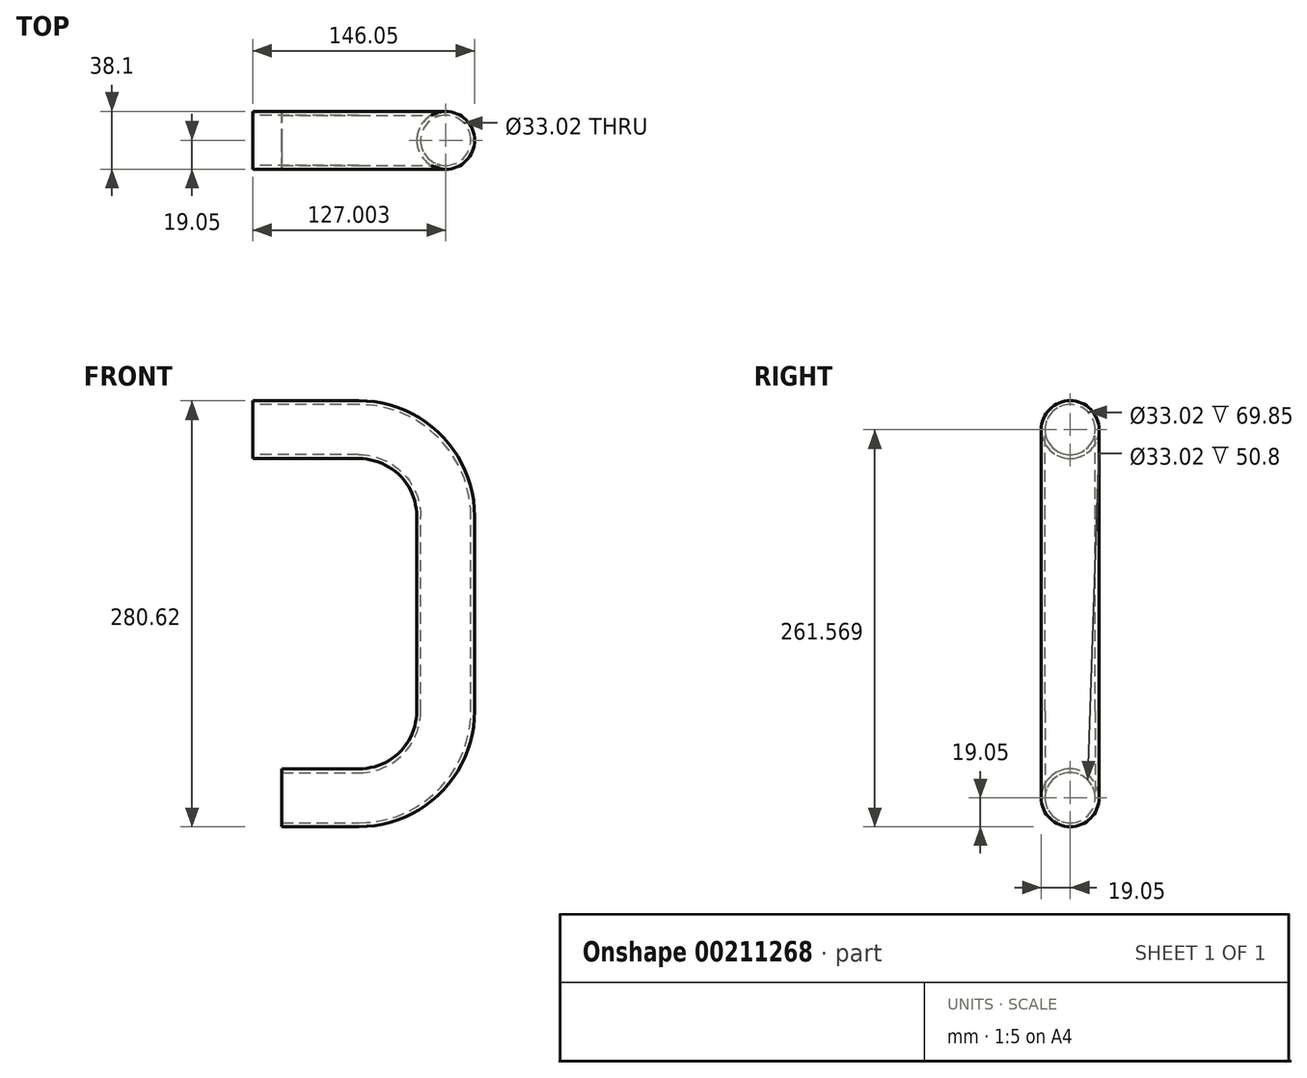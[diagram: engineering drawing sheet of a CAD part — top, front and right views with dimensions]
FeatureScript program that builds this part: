
annotation { "Feature Type Name" : "Feature", "Feature Type Description" : "" }
export const myFeature = defineFeature(function(context is Context, id is Id, definition is map)
    precondition{}
    {
        {
            var Q0;
            Q0=qCreatedBy(makeId("Front.planeOp"),FACE);
            var sketch = newSketch(context, id + "F0", { "sketchPlane" : qUnion([Q0])});
            skLineSegment(sketch, "E0", {"start": v(-64.1, 0) * mm, "end": v(-64.1, 19.05) * mm});
            skLineSegment(sketch, "E1", {"start": v(-64.1, 19.05) * mm, "end": v(-13.3, 19.05) * mm});
            skLineSegment(sketch, "E2", {"start": v(24.8, 57.15) * mm, "end": v(24.8, 185.37) * mm});
            skLineSegment(sketch, "E3", {"start": v(-13.3, 223.47) * mm, "end": v(-83.15, 223.47) * mm});
            skLineSegment(sketch, "E4", {"start": v(-83.15, 223.47) * mm, "end": v(-83.15, 261.57) * mm});
            skLineSegment(sketch, "E5", {"start": v(-83.15, 261.57) * mm, "end": v(-13.3, 261.57) * mm});
            skLineSegment(sketch, "E6", {"start": v(62.9, 185.37) * mm, "end": v(62.9, 57.15) * mm});
            skLineSegment(sketch, "E7", {"start": v(-13.3, -19.05) * mm, "end": v(-64.1, -19.05) * mm});
            skLineSegment(sketch, "E8", {"start": v(-64.1, -19.05) * mm, "end": v(-64.1, 0) * mm});
            skPoint(sketch, "E9.visualSharp", {"position": v(24.8, 223.47) * mm});
            skArc(sketch, "E9.filletArc", {"start": v(24.8, 185.37) * mm, "mid": v(13.64, 212.3) * mm, "end": v(-13.3, 223.47) * mm});
            skPoint(sketch, "E10.visualSharp", {"position": v(24.8, 19.05) * mm});
            skArc(sketch, "E10.filletArc", {"start": v(-13.3, 19.05) * mm, "mid": v(13.64, 30.2) * mm, "end": v(24.8, 57.15) * mm});
            skPoint(sketch, "E11.visualSharp", {"position": v(62.9, 261.57) * mm});
            skArc(sketch, "E11.filletArc", {"start": v(62.9, 185.37) * mm, "mid": v(40.58, 239.25) * mm, "end": v(-13.3, 261.57) * mm});
            skPoint(sketch, "E12.visualSharp", {"position": v(62.9, -19.05) * mm});
            skArc(sketch, "E12.filletArc", {"start": v(-13.3, -19.05) * mm, "mid": v(40.58, 3.27) * mm, "end": v(62.9, 57.15) * mm});
            skSolve(sketch);
        }
        {
            var Q0;
            Q0 = qSketchRegion(id + "F0", true);
            extrude(context, id + "F1", {"entities" : qUnion([Q0]), "depth" : 38.1 * mm});
        }
        {
            var Q0;
            Q0=makeQuery(id+"F1.opExtrude","CAP_EDGE",EDGE,{"disambiguationData":[OSD([sQuery(id+"F0.wireOp",EDGE,"E5")])],"isStart":false});
            var Q1;
            Q1=makeQuery(id+"F1.opExtrude","CAP_EDGE",EDGE,{"disambiguationData":[OSD([sQuery(id+"F0.wireOp",EDGE,"E3")])],"isStart":false});
            var Q2;
            Q2=makeQuery(id+"F1.opExtrude","CAP_EDGE",EDGE,{"disambiguationData":[OSD([sQuery(id+"F0.wireOp",EDGE,"E3")])],"isStart":true});
            var Q3;
            Q3=makeQuery(id+"F1.opExtrude","CAP_EDGE",EDGE,{"disambiguationData":[OSD([sQuery(id+"F0.wireOp",EDGE,"E5")])],"isStart":true});
            fillet(context, id + "F2", {"entities" : qUnion([Q0, Q1, Q2, Q3]), "radius" : 19.05 * mm, "tangentPropagation" : true, "allowEdgeOverflow" : false});
        }
        {
            var Q0;
            Q0=makeQuery(id+"F1.opExtrude","SWEPT_FACE",FACE,{"disambiguationData":[OSD([sQuery(id+"F0.wireOp",EDGE,"E4")])]});
            var Q1;
            Q1=makeQuery(id+"F1.opExtrude","SWEPT_FACE",FACE,{"disambiguationData":[OSD([sQuery(id+"F0.wireOp",EDGE,"E0"),sQuery(id+"F0.wireOp",EDGE,"E8")])]});
            shell(context, id + "F3", {"entities" : qUnion([Q0, Q1]), "thickness" : 2.54 * mm});
        }
    });
